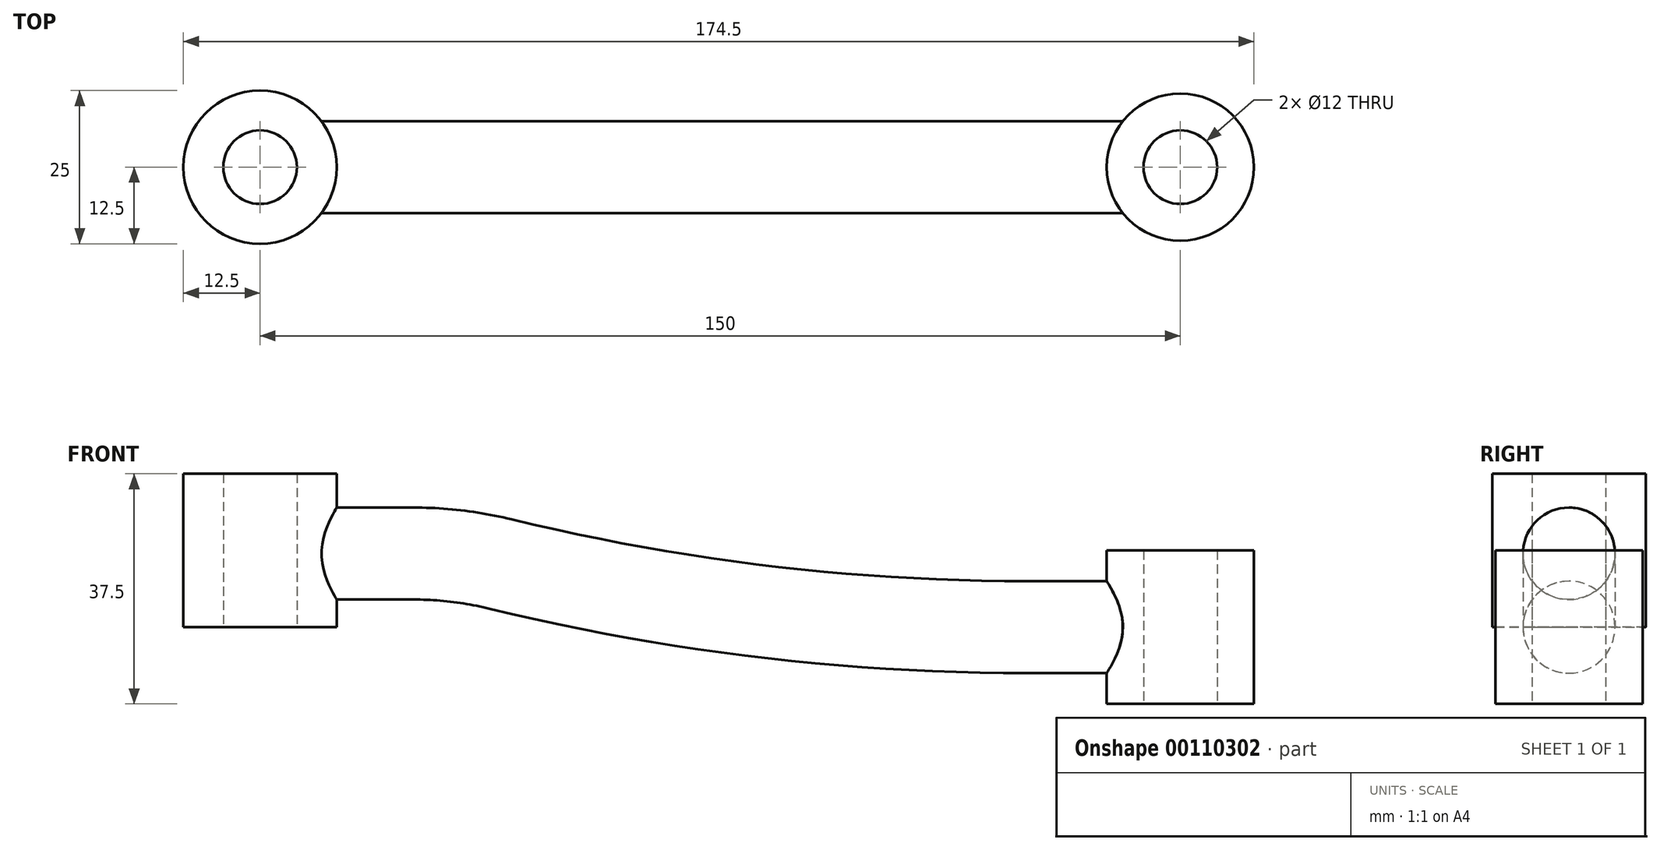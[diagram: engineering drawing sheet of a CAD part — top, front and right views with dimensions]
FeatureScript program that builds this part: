
annotation { "Feature Type Name" : "Feature", "Feature Type Description" : "" }
export const myFeature = defineFeature(function(context is Context, id is Id, definition is map)
    precondition{}
    {
        {
            var Q0;
            Q0=qCreatedBy(makeId("Top.planeOp"),FACE);
            var sketch = newSketch(context, id + "F0", { "sketchPlane" : qUnion([Q0])});
            skCircle(sketch, "E0", {"center": v(0, 0) * mm, "radius": 6 * mm});
            skCircle(sketch, "E1", {"center": v(0, 0) * mm, "radius": 12.5 * mm});
            skSolve(sketch);
        }
        {
            var Q0;
            Q0 = qSketchRegion(id + "F0", true);
            extrude(context, id + "F1", {"entities" : qUnion([Q0]), "depth" : 25 * mm});
        }
        {
            var Q0;
            Q0=qCreatedBy(makeId("Front.planeOp"),FACE);
            var sketch = newSketch(context, id + "F2", { "sketchPlane" : qUnion([Q0])});
            skLineSegment(sketch, "E2", {"start": v(0, 12) * mm, "end": v(25, 12) * mm});
            skArc(sketch, "E3", {"start": v(39.2, 10.3) * mm, "mid": v(32.15, 11.57) * mm, "end": v(25, 12) * mm});
            skArc(sketch, "E4", {"start": v(39.2, 10.3) * mm, "mid": v(81.79, 2.58) * mm, "end": v(125, 0) * mm});
            skLineSegment(sketch, "E5", {"start": v(125, 0) * mm, "end": v(150, 0) * mm});
            skSolve(sketch);
        }
        {
            var Q0;
            Q0=qCreatedBy(makeId("Top.planeOp"),FACE);
            var sketch = newSketch(context, id + "F3", { "sketchPlane" : qUnion([Q0])});
            skCircle(sketch, "E6", {"center": v(150, 0) * mm, "radius": 12 * mm});
            skCircle(sketch, "E7", {"center": v(150, 0) * mm, "radius": 6 * mm});
            skSolve(sketch);
        }
        {
            var Q0;
            Q0 = qSketchRegion(id + "F3", true);
            extrude(context, id + "F4", {"entities" : qUnion([Q0]), "depth" : 12.5 * mm, "hasSecondDirection" : true, "secondDirectionOppositeDirection" : true, "secondDirectionDepth" : 12.5 * mm});
        }
        {
            var Q0;
            Q0=qCreatedBy(makeId("Right.planeOp"),FACE);
            var sketch = newSketch(context, id + "F5", { "sketchPlane" : qUnion([Q0])});
            skCircle(sketch, "E8", {"center": v(0, 12) * mm, "radius": 7.5 * mm});
            skSolve(sketch);
        }
        {
            var Q0;
            Q0 = qSketchRegion(id + "F5", true);
            var Q1;
            Q1=sQuery(id+"F2.wireOp",EDGE,"E2");
            var Q2;
            Q2=sQuery(id+"F2.wireOp",EDGE,"E3");
            var Q3;
            Q3=sQuery(id+"F2.wireOp",EDGE,"E4");
            var Q4;
            Q4=sQuery(id+"F2.wireOp",EDGE,"E5");
            sweep(context, id + "F6", {"operationType" : NewBodyOperationType.ADD, "profiles" : qUnion([Q0]), "path" : qUnion([Q1, Q2, Q3, Q4])});
        }
        {
            var Q0;
            Q0=qCreatedBy(makeId("Top.planeOp"),FACE);
            var sketch = newSketch(context, id + "F7", { "sketchPlane" : qUnion([Q0])});
            skCircle(sketch, "E9", {"center": v(0, 0) * mm, "radius": 6 * mm});
            skCircle(sketch, "E10", {"center": v(150, 0) * mm, "radius": 6 * mm});
            skSolve(sketch);
        }
        {
            var Q0;
            Q0 = qSketchRegion(id + "F7", true);
            extrude(context, id + "F8", {"entities" : qUnion([Q0]), "operationType" : NewBodyOperationType.REMOVE, "endBound" : BoundingType.THROUGH_ALL, "oppositeDirection" : true, "depth" : 25 * mm, "hasSecondDirection" : true, "secondDirectionBound" : SecondDirectionBoundingType.THROUGH_ALL, "secondDirectionOppositeDirection" : false, "secondDirectionDepth" : 25 * mm});
        }
    });
